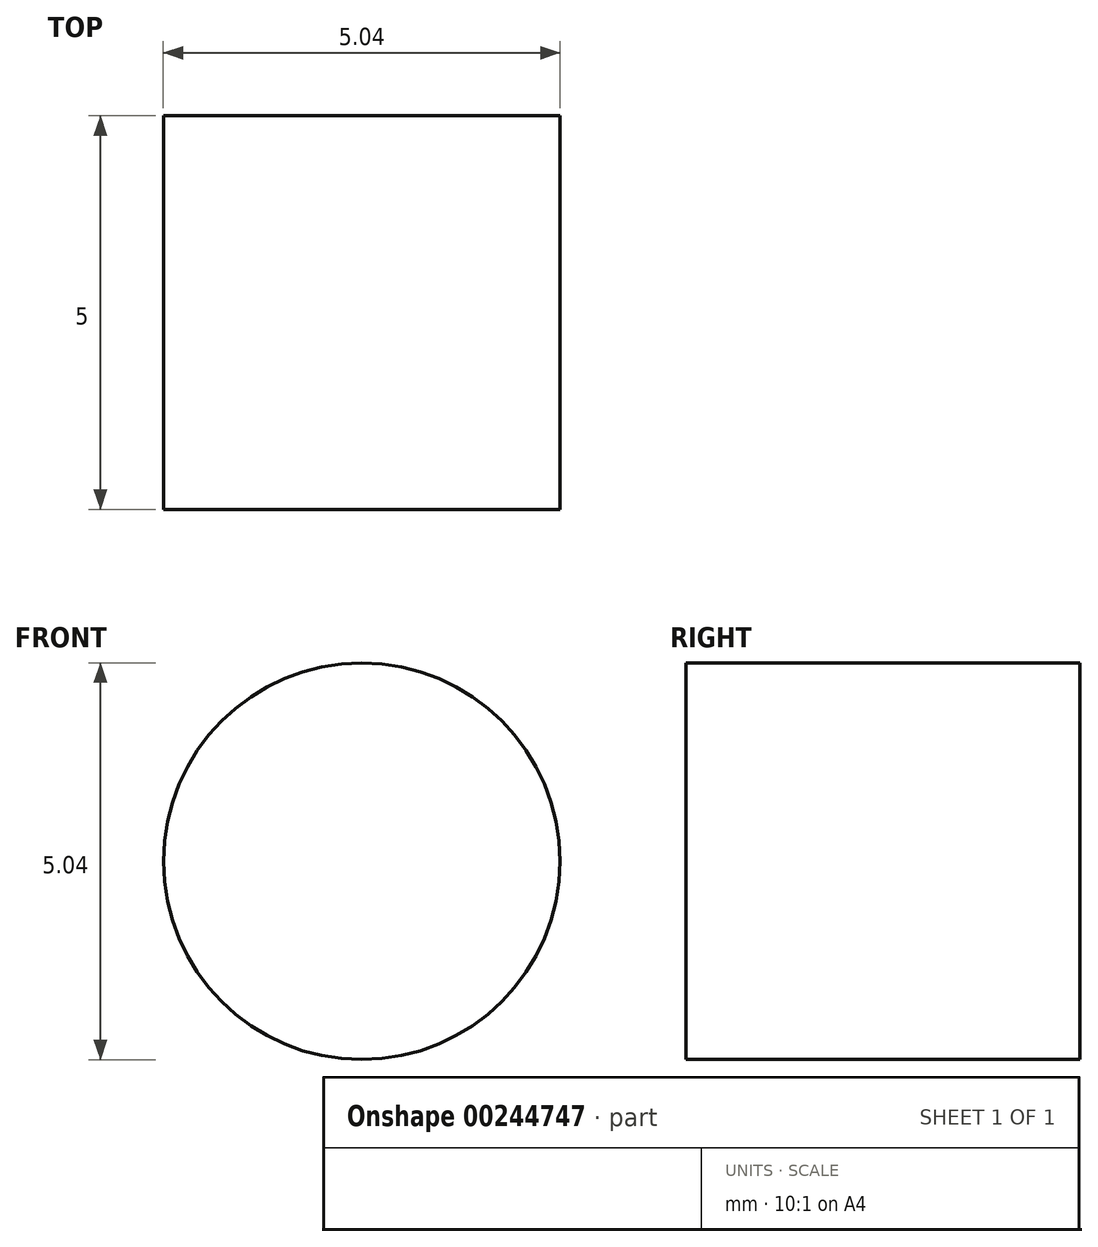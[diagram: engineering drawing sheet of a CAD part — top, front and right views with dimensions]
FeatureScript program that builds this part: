
annotation { "Feature Type Name" : "Feature", "Feature Type Description" : "" }
export const myFeature = defineFeature(function(context is Context, id is Id, definition is map)
    precondition{}
    {
        {
            var Q0;
            Q0=qCreatedBy(makeId("Front.planeOp"),FACE);
            var sketch = newSketch(context, id + "F0", { "sketchPlane" : qUnion([Q0])});
            skCircle(sketch, "E0", {"center": v(0, 0) * mm, "radius": 2.52 * mm});
            skSolve(sketch);
        }
        {
            var Q0;
            Q0 = qSketchRegion(id + "F0", true);
            extrude(context, id + "F1", {"entities" : qUnion([Q0]), "depth" : 5 * mm});
        }
    });
